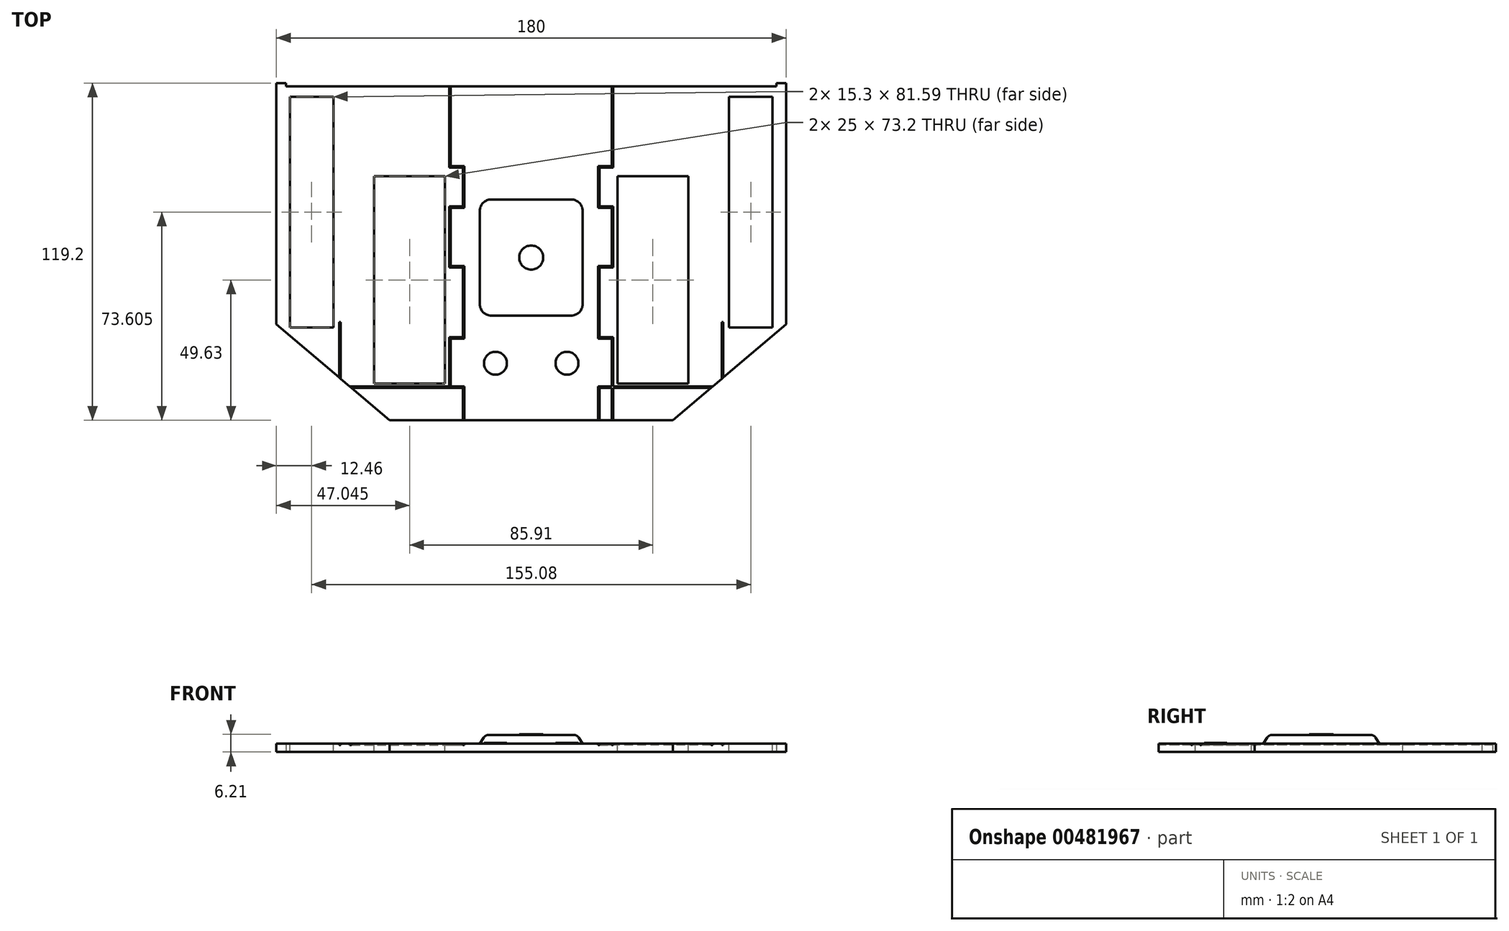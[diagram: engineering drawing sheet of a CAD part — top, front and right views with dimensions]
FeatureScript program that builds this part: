
annotation { "Feature Type Name" : "Feature", "Feature Type Description" : "" }
export const myFeature = defineFeature(function(context is Context, id is Id, definition is map)
    precondition{}
    {
        {
            var Q0;
            Q0=qCreatedBy(makeId("Top.planeOp"),FACE);
            var sketch = newSketch(context, id + "F0", { "sketchPlane" : qUnion([Q0])});
            skLineSegment(sketch, "E0", {"start": v(-90, 48.44) * mm, "end": v(-86.6, 48.44) * mm});
            skLineSegment(sketch, "E1", {"start": v(90, 48.44) * mm, "end": v(90, -36.76) * mm});
            skLineSegment(sketch, "E2", {"start": v(90, -36.76) * mm, "end": v(50, -70.76) * mm});
            skLineSegment(sketch, "E3", {"start": v(50, -70.76) * mm, "end": v(-50, -70.76) * mm});
            skLineSegment(sketch, "E4", {"start": v(-50, -70.76) * mm, "end": v(-90, -36.76) * mm});
            skLineSegment(sketch, "E5", {"start": v(-90, -36.76) * mm, "end": v(-90, 48.44) * mm});
            skLineSegment(sketch, "E6.0", {"start": v(-86.6, 47.34) * mm, "end": v(86.6, 47.34) * mm});
            skLineSegment(sketch, "E7.0", {"start": v(86.6, 48.44) * mm, "end": v(86.6, 47.34) * mm});
            skLineSegment(sketch, "E8.0", {"start": v(-86.6, 47.34) * mm, "end": v(-86.6, 48.44) * mm});
            skLineSegment(sketch, "E9.trimOffspring", {"start": v(86.6, 48.44) * mm, "end": v(90, 48.44) * mm});
            skLineSegment(sketch, "E10", {"start": v(0, 47.34) * mm, "end": v(0, -70.76) * mm, "construction": true});
            skSolve(sketch);
        }
        {
            var Q0;
            Q0 = qSketchRegion(id + "F0", true);
            extrude(context, id + "F1", {"entities" : qUnion([Q0]), "depth" : 3 * mm});
        }
        {
            var Q0;
            Q0=makeQuery(id+"F1.opExtrude","CAP_FACE",FACE,{"disambiguationData":[OSD([sQuery(id+"F0.wireOp",EDGE,"E0"),sQuery(id+"F0.wireOp",EDGE,"E1"),sQuery(id+"F0.wireOp",EDGE,"E2"),sQuery(id+"F0.wireOp",EDGE,"E3"),sQuery(id+"F0.wireOp",EDGE,"E4"),sQuery(id+"F0.wireOp",EDGE,"E5"),sQuery(id+"F0.wireOp",EDGE,"E6.0"),sQuery(id+"F0.wireOp",EDGE,"E7.0"),sQuery(id+"F0.wireOp",EDGE,"E8.0"),sQuery(id+"F0.wireOp",EDGE,"E9.trimOffspring")])],"isStart":false});
            var sketch = newSketch(context, id + "F2", { "sketchPlane" : qUnion([Q0])});
            skLineSegment(sketch, "E11", {"start": v(0, 47.34) * mm, "end": v(0, -70.76) * mm, "construction": true});
            skLineSegment(sketch, "E12", {"start": v(28.9, 47.34) * mm, "end": v(-28.9, 47.34) * mm});
            skLineSegment(sketch, "E13", {"start": v(28.9, 47.34) * mm, "end": v(28.9, 18.62) * mm});
            skLineSegment(sketch, "E14", {"start": v(28.9, 18.62) * mm, "end": v(24.1, 18.62) * mm});
            skLineSegment(sketch, "E15", {"start": v(24.1, 18.62) * mm, "end": v(24.1, 4.84) * mm});
            skLineSegment(sketch, "E16", {"start": v(24.1, 4.84) * mm, "end": v(28.9, 4.84) * mm});
            skLineSegment(sketch, "E17", {"start": v(28.9, 4.84) * mm, "end": v(28.9, -16.68) * mm});
            skLineSegment(sketch, "E18", {"start": v(28.9, -16.68) * mm, "end": v(24.1, -16.68) * mm});
            skLineSegment(sketch, "E19", {"start": v(24.1, -16.68) * mm, "end": v(24.1, -41.33) * mm});
            skLineSegment(sketch, "E20", {"start": v(24.1, -41.33) * mm, "end": v(28.9, -41.33) * mm});
            skLineSegment(sketch, "E21", {"start": v(28.9, -41.33) * mm, "end": v(28.9, -58.78) * mm});
            skLineSegment(sketch, "E22", {"start": v(67.82, -59.28) * mm, "end": v(28.9, -59.28) * mm});
            skLineSegment(sketch, "E23", {"start": v(24.1, -59.28) * mm, "end": v(24.1, -70.76) * mm});
            skLineSegment(sketch, "E24.0", {"start": v(23.6, -58.78) * mm, "end": v(23.6, -70.76) * mm});
            skLineSegment(sketch, "E24.1", {"start": v(23.6, 4.34) * mm, "end": v(28.4, 4.34) * mm});
            skLineSegment(sketch, "E24.2", {"start": v(23.6, 19.12) * mm, "end": v(23.6, 4.34) * mm});
            skLineSegment(sketch, "E24.3", {"start": v(28.4, 19.12) * mm, "end": v(23.6, 19.12) * mm});
            skLineSegment(sketch, "E24.4", {"start": v(28.4, 47.34) * mm, "end": v(28.4, 19.12) * mm});
            skLineSegment(sketch, "E24.5", {"start": v(28.4, 4.34) * mm, "end": v(28.4, -16.18) * mm});
            skLineSegment(sketch, "E24.6", {"start": v(28.4, -16.18) * mm, "end": v(23.6, -16.18) * mm});
            skLineSegment(sketch, "E24.7", {"start": v(23.6, -16.18) * mm, "end": v(23.6, -41.83) * mm});
            skLineSegment(sketch, "E24.8", {"start": v(23.6, -41.83) * mm, "end": v(28.4, -41.83) * mm});
            skLineSegment(sketch, "E24.9", {"start": v(28.4, -41.83) * mm, "end": v(28.4, -58.78) * mm});
            skLineSegment(sketch, "E24.10", {"start": v(67.32, -58.78) * mm, "end": v(28.9, -58.78) * mm});
            skLineSegment(sketch, "E25", {"start": v(23.6, -70.76) * mm, "end": v(24.1, -70.76) * mm});
            skLineSegment(sketch, "E26", {"start": v(28.4, 47.34) * mm, "end": v(28.9, 47.34) * mm});
            skLineSegment(sketch, "E27.MirrorCS", {"start": v(-28.4, 47.34) * mm, "end": v(-28.9, 47.34) * mm});
            skLineSegment(sketch, "E28.MirrorCS", {"start": v(-28.9, -16.68) * mm, "end": v(-24.1, -16.68) * mm});
            skLineSegment(sketch, "E29.MirrorCS", {"start": v(-28.4, -16.18) * mm, "end": v(-23.6, -16.18) * mm});
            skLineSegment(sketch, "E30.MirrorCS", {"start": v(-28.4, -58.78) * mm, "end": v(-23.6, -58.78) * mm});
            skLineSegment(sketch, "E31.MirrorCS", {"start": v(-23.6, -70.76) * mm, "end": v(-24.1, -70.76) * mm});
            skLineSegment(sketch, "E32.MirrorCS", {"start": v(-28.9, 18.62) * mm, "end": v(-24.1, 18.62) * mm});
            skLineSegment(sketch, "E33.MirrorCS", {"start": v(-24.1, 4.84) * mm, "end": v(-28.9, 4.84) * mm});
            skLineSegment(sketch, "E34.MirrorCS", {"start": v(-28.4, 19.12) * mm, "end": v(-23.6, 19.12) * mm});
            skLineSegment(sketch, "E35.MirrorCS", {"start": v(-24.1, -41.33) * mm, "end": v(-28.9, -41.33) * mm});
            skLineSegment(sketch, "E36.MirrorCS", {"start": v(-28.9, -59.28) * mm, "end": v(-24.1, -59.28) * mm});
            skLineSegment(sketch, "E37.MirrorCS", {"start": v(-23.6, 4.34) * mm, "end": v(-28.4, 4.34) * mm});
            skLineSegment(sketch, "E38.MirrorCS", {"start": v(-23.6, -41.83) * mm, "end": v(-28.4, -41.83) * mm});
            skLineSegment(sketch, "E39.MirrorCS", {"start": v(-28.9, 47.34) * mm, "end": v(-28.9, 18.62) * mm});
            skLineSegment(sketch, "E40.MirrorCS", {"start": v(-23.6, -58.78) * mm, "end": v(-23.6, -70.76) * mm});
            skLineSegment(sketch, "E41.MirrorCS", {"start": v(-24.1, -59.28) * mm, "end": v(-24.1, -70.76) * mm});
            skLineSegment(sketch, "E42.MirrorCS", {"start": v(-28.9, -41.33) * mm, "end": v(-28.9, -59.28) * mm});
            skLineSegment(sketch, "E43.MirrorCS", {"start": v(-28.9, 4.84) * mm, "end": v(-28.9, -16.68) * mm});
            skLineSegment(sketch, "E44.MirrorCS", {"start": v(-23.6, 19.12) * mm, "end": v(-23.6, 4.34) * mm});
            skLineSegment(sketch, "E45.MirrorCS", {"start": v(-23.6, -16.18) * mm, "end": v(-23.6, -41.83) * mm});
            skLineSegment(sketch, "E46.MirrorCS", {"start": v(-28.4, -41.83) * mm, "end": v(-28.4, -58.78) * mm});
            skLineSegment(sketch, "E47.MirrorCS", {"start": v(-28.4, 4.34) * mm, "end": v(-28.4, -16.18) * mm});
            skLineSegment(sketch, "E48.MirrorCS", {"start": v(-24.1, -16.68) * mm, "end": v(-24.1, -41.33) * mm});
            skLineSegment(sketch, "E49.MirrorCS", {"start": v(-28.4, 47.34) * mm, "end": v(-28.4, 19.12) * mm});
            skLineSegment(sketch, "E50.MirrorCS", {"start": v(-24.1, 18.62) * mm, "end": v(-24.1, 4.84) * mm});
            skPoint(sketch, "E51.orphan", {"position": v(28.9, -59.28) * mm});
            skPoint(sketch, "E52.orphan", {"position": v(28.4, -58.78) * mm});
            skLineSegment(sketch, "E53", {"start": v(67.32, -58.78) * mm, "end": v(67.32, -36) * mm});
            skLineSegment(sketch, "E54.0", {"start": v(67.82, -59.28) * mm, "end": v(67.82, -36) * mm});
            skLineSegment(sketch, "E55", {"start": v(67.32, -36) * mm, "end": v(67.82, -36) * mm});
            skLineSegment(sketch, "E56.trimOffspring", {"start": v(28.4, -58.78) * mm, "end": v(23.6, -58.78) * mm});
            skLineSegment(sketch, "E57.trimOffspring", {"start": v(28.4, -59.28) * mm, "end": v(28.4, -71.66) * mm});
            skLineSegment(sketch, "E58.trimOffspring", {"start": v(28.4, -59.28) * mm, "end": v(24.1, -59.28) * mm});
            skLineSegment(sketch, "E59.trimOffspring", {"start": v(28.9, -59.28) * mm, "end": v(28.9, -71.7) * mm});
            skLineSegment(sketch, "E60", {"start": v(28.4, -71.66) * mm, "end": v(28.9, -71.7) * mm});
            skLineSegment(sketch, "E61.MirrorCS", {"start": v(-67.32, -36) * mm, "end": v(-67.82, -36) * mm});
            skLineSegment(sketch, "E62.MirrorCS", {"start": v(-67.32, -58.78) * mm, "end": v(-67.32, -36) * mm});
            skLineSegment(sketch, "E63.MirrorCS", {"start": v(-67.82, -59.28) * mm, "end": v(-67.82, -36) * mm});
            skLineSegment(sketch, "E64.MirrorCS", {"start": v(-67.82, -59.28) * mm, "end": v(-28.9, -59.28) * mm});
            skLineSegment(sketch, "E65.MirrorCS", {"start": v(-67.32, -58.78) * mm, "end": v(-28.9, -58.78) * mm});
            skLineSegment(sketch, "E66.MirrorCS", {"start": v(-28.4, -59.28) * mm, "end": v(-28.4, -71.66) * mm});
            skLineSegment(sketch, "E67.MirrorCS", {"start": v(-28.9, -59.28) * mm, "end": v(-28.9, -71.7) * mm});
            skSolve(sketch);
        }
        {
            var Q0;
            Q0 = qSketchRegion(id + "F2", true);
            extrude(context, id + "F3", {"entities" : qUnion([Q0]), "operationType" : NewBodyOperationType.REMOVE, "oppositeDirection" : true, "depth" : .5 * mm});
        }
        {
            var Q0;
            {var subQ0=sQuery(id+"F0.wireOp",EDGE,"E6.0");var subQ1=sQuery(id+"F0.wireOp",EDGE,"E3");Q0=makeQuery(id+"F3.boolean.opBoolean","SPLIT",FACE,{"disambiguationData":[TD([makeQuery(id+"F3.opExtrude","SWEPT_FACE",FACE,{"disambiguationData":[OSD([sQuery(id+"F2.wireOp",EDGE,"E24.0")])]})])],"derivedFrom":makeQuery(id+"F1.opExtrude","CAP_FACE",FACE,{"disambiguationData":[OSD([sQuery(id+"F0.wireOp",EDGE,"E0"),sQuery(id+"F0.wireOp",EDGE,"E1"),sQuery(id+"F0.wireOp",EDGE,"E2"),subQ1,sQuery(id+"F0.wireOp",EDGE,"E4"),sQuery(id+"F0.wireOp",EDGE,"E5"),subQ0,sQuery(id+"F0.wireOp",EDGE,"E7.0"),sQuery(id+"F0.wireOp",EDGE,"E8.0"),sQuery(id+"F0.wireOp",EDGE,"E9.trimOffspring")])],"isStart":false})});}
            var sketch = newSketch(context, id + "F4", { "sketchPlane" : qUnion([Q0])});
            skLineSegment(sketch, "E68", {"start": v(0, -70.76) * mm, "end": v(0, -13.21) * mm, "construction": true});
            skPoint(sketch, "E68.endSnap0", {"position": v(0, -70.76) * mm});
            skLineSegment(sketch, "E69.bottom", {"start": v(-14.12, 7.31) * mm, "end": v(14.11, 7.31) * mm});
            skLineSegment(sketch, "E69.top", {"start": v(-14.12, -33.74) * mm, "end": v(14.11, -33.74) * mm});
            skLineSegment(sketch, "E69.left", {"start": v(-18.16, 3.27) * mm, "end": v(-18.16, -29.7) * mm});
            skLineSegment(sketch, "E69.right", {"start": v(18.16, 3.27) * mm, "end": v(18.15, -29.7) * mm});
            skPoint(sketch, "E69.middle", {"position": v(0, -13.21) * mm});
            skPoint(sketch, "E70.visualSharp", {"position": v(-18.16, 7.31) * mm});
            skArc(sketch, "E70.filletArc", {"start": v(-14.12, 7.31) * mm, "mid": v(-16.97, 6.13) * mm, "end": v(-18.16, 3.27) * mm});
            skPoint(sketch, "E71.visualSharp", {"position": v(18.16, 7.31) * mm});
            skArc(sketch, "E71.filletArc", {"start": v(18.15, 3.27) * mm, "mid": v(16.97, 6.13) * mm, "end": v(14.11, 7.31) * mm});
            skPoint(sketch, "E72.visualSharp", {"position": v(18.15, -33.74) * mm});
            skArc(sketch, "E72.filletArc", {"start": v(14.11, -33.74) * mm, "mid": v(16.97, -32.55) * mm, "end": v(18.16, -29.7) * mm});
            skPoint(sketch, "E73.visualSharp", {"position": v(-18.16, -33.74) * mm});
            skArc(sketch, "E73.filletArc", {"start": v(-18.16, -29.7) * mm, "mid": v(-16.97, -32.55) * mm, "end": v(-14.12, -33.74) * mm});
            skSolve(sketch);
        }
        {
            var Q0;
            Q0 = qSketchRegion(id + "F4", true);
            extrude(context, id + "F5", {"entities" : qUnion([Q0]), "operationType" : NewBodyOperationType.ADD, "depth" : 3 * mm});
        }
        {
            var Q0;
            Q0=makeQuery(id+"F5.opExtrude","CAP_EDGE",EDGE,{"disambiguationData":[OSD([sQuery(id+"F4.wireOp",EDGE,"E69.left")])],"isStart":false});
            chamfer(context, id + "F6", {"entities" : qUnion([Q0]), "chamferType" : ChamferType.TWO_OFFSETS, "width1" : 2 * mm, "oppositeDirection" : false, "width2" : 3 * mm, "tangentPropagation" : true});
        }
        {
            var Q0;
            {var subQ0=sQuery(id+"F4.wireOp",EDGE,"E71.filletArc");Q0=makeQuery(id+"F6.opChamfer","BLEND_EDGE",EDGE,{"blendedFrom":[makeQuery(id+"F5.opExtrude","CAP_EDGE",EDGE,{"disambiguationData":[OSD([subQ0])],"isStart":false}),makeQuery(id+"F5.opExtrude","CAP_FACE",FACE,{"disambiguationData":[OSD([sQuery(id+"F4.wireOp",EDGE,"E69.bottom"),sQuery(id+"F4.wireOp",EDGE,"E69.top"),sQuery(id+"F4.wireOp",EDGE,"E69.left"),sQuery(id+"F4.wireOp",EDGE,"E69.right"),sQuery(id+"F4.wireOp",EDGE,"E70.filletArc"),subQ0,sQuery(id+"F4.wireOp",EDGE,"E72.filletArc"),sQuery(id+"F4.wireOp",EDGE,"E73.filletArc")])],"isStart":false})],"blendedInto":[makeQuery(id+"F5.opExtrude","CAP_FACE",FACE,{"disambiguationData":[OSD([sQuery(id+"F4.wireOp",EDGE,"E69.bottom"),sQuery(id+"F4.wireOp",EDGE,"E69.top"),sQuery(id+"F4.wireOp",EDGE,"E69.left"),sQuery(id+"F4.wireOp",EDGE,"E69.right"),sQuery(id+"F4.wireOp",EDGE,"E70.filletArc"),subQ0,sQuery(id+"F4.wireOp",EDGE,"E72.filletArc"),sQuery(id+"F4.wireOp",EDGE,"E73.filletArc")])],"isStart":false})]});}
            fillet(context, id + "F7", {"entities" : qUnion([Q0]), "radius" : 2 * mm, "tangentPropagation" : true, "allowEdgeOverflow" : false});
        }
        {
            var Q0;
            Q0=makeQuery(id+"F5.opExtrude","CAP_FACE",FACE,{"disambiguationData":[OSD([sQuery(id+"F4.wireOp",EDGE,"E69.bottom"),sQuery(id+"F4.wireOp",EDGE,"E69.top"),sQuery(id+"F4.wireOp",EDGE,"E69.left"),sQuery(id+"F4.wireOp",EDGE,"E69.right"),sQuery(id+"F4.wireOp",EDGE,"E70.filletArc"),sQuery(id+"F4.wireOp",EDGE,"E71.filletArc"),sQuery(id+"F4.wireOp",EDGE,"E72.filletArc"),sQuery(id+"F4.wireOp",EDGE,"E73.filletArc")])],"isStart":false});
            var sketch = newSketch(context, id + "F8", { "sketchPlane" : qUnion([Q0])});
            skLineSegment(sketch, "E74", {"start": v(0, -30.66) * mm, "end": v(0, 4.24) * mm, "construction": true});
            skCircle(sketch, "E75", {"center": v(0, -13.21) * mm, "radius": 4.25 * mm});
            skSolve(sketch);
        }
        {
            var Q0;
            Q0 = qSketchRegion(id + "F8", true);
            extrude(context, id + "F9", {"entities" : qUnion([Q0]), "operationType" : NewBodyOperationType.ADD, "depth" : .2 * mm});
        }
        {
            var Q0;
            {var subQ0=sQuery(id+"F0.wireOp",EDGE,"E6.0");var subQ1=sQuery(id+"F0.wireOp",EDGE,"E3");Q0=makeQuery(id+"F3.boolean.opBoolean","SPLIT",FACE,{"disambiguationData":[TD([makeQuery(id+"F3.opExtrude","SWEPT_FACE",FACE,{"disambiguationData":[OSD([sQuery(id+"F2.wireOp",EDGE,"E24.0")])]})])],"derivedFrom":makeQuery(id+"F1.opExtrude","CAP_FACE",FACE,{"disambiguationData":[OSD([sQuery(id+"F0.wireOp",EDGE,"E0"),sQuery(id+"F0.wireOp",EDGE,"E1"),sQuery(id+"F0.wireOp",EDGE,"E2"),subQ1,sQuery(id+"F0.wireOp",EDGE,"E4"),sQuery(id+"F0.wireOp",EDGE,"E5"),subQ0,sQuery(id+"F0.wireOp",EDGE,"E7.0"),sQuery(id+"F0.wireOp",EDGE,"E8.0"),sQuery(id+"F0.wireOp",EDGE,"E9.trimOffspring")])],"isStart":false})});}
            var sketch = newSketch(context, id + "F10", { "sketchPlane" : qUnion([Q0])});
            skLineSegment(sketch, "E76", {"start": v(0, -70.76) * mm, "end": v(0, -50.57) * mm, "construction": true});
            skLineSegment(sketch, "E77", {"start": v(-12.63, -50.57) * mm, "end": v(12.63, -50.57) * mm, "construction": true});
            skCircle(sketch, "E78", {"center": v(-12.63, -50.57) * mm, "radius": 4.04 * mm});
            skCircle(sketch, "E79", {"center": v(12.63, -50.57) * mm, "radius": 4.04 * mm});
            skSolve(sketch);
        }
        {
            var Q0;
            Q0 = qSketchRegion(id + "F10", true);
            extrude(context, id + "F11", {"entities" : qUnion([Q0]), "operationType" : NewBodyOperationType.ADD, "depth" : .2 * mm});
        }
        {
            var Q0;
            {var subQ0=sQuery(id+"F0.wireOp",EDGE,"E8.0");var subQ1=sQuery(id+"F0.wireOp",EDGE,"E6.0");var subQ2=sQuery(id+"F0.wireOp",EDGE,"E0");var subQ3=sQuery(id+"F0.wireOp",EDGE,"E3");var subQ4=sQuery(id+"F0.wireOp",EDGE,"E4");var subQ5=sQuery(id+"F0.wireOp",EDGE,"E5");Q0=makeQuery(id+"F3.boolean.opBoolean","SPLIT",FACE,{"disambiguationData":[TD([makeQuery(id+"F1.opExtrude","SWEPT_FACE",FACE,{"disambiguationData":[OSD([subQ2])]})])],"derivedFrom":makeQuery(id+"F1.opExtrude","CAP_FACE",FACE,{"disambiguationData":[OSD([subQ2,sQuery(id+"F0.wireOp",EDGE,"E1"),sQuery(id+"F0.wireOp",EDGE,"E2"),subQ3,subQ4,subQ5,subQ1,sQuery(id+"F0.wireOp",EDGE,"E7.0"),subQ0,sQuery(id+"F0.wireOp",EDGE,"E9.trimOffspring")])],"isStart":false})});}
            var sketch = newSketch(context, id + "F12", { "sketchPlane" : qUnion([Q0])});
            skLineSegment(sketch, "E80", {"start": v(0, 0) * mm, "end": v(0, -56.54) * mm, "construction": true});
            skLineSegment(sketch, "E81.bottom", {"start": v(-85.19, 43.64) * mm, "end": v(-69.9, 43.64) * mm});
            skLineSegment(sketch, "E81.top", {"start": v(-85.19, -37.95) * mm, "end": v(-69.9, -37.95) * mm});
            skLineSegment(sketch, "E81.left", {"start": v(-85.2, 43.64) * mm, "end": v(-85.19, -37.95) * mm});
            skLineSegment(sketch, "E81.right", {"start": v(-69.89, 43.64) * mm, "end": v(-69.89, -37.95) * mm});
            skLineSegment(sketch, "E82.MirrorCS", {"start": v(69.89, 43.64) * mm, "end": v(69.89, -37.95) * mm});
            skLineSegment(sketch, "E83.MirrorCS", {"start": v(85.19, 43.64) * mm, "end": v(69.89, 43.64) * mm});
            skLineSegment(sketch, "E84.MirrorCS", {"start": v(85.19, 43.64) * mm, "end": v(85.19, -37.95) * mm});
            skLineSegment(sketch, "E85.MirrorCS", {"start": v(85.19, -37.95) * mm, "end": v(69.9, -37.95) * mm});
            skLineSegment(sketch, "E86.0", {"start": v(-55.45, -57.73) * mm, "end": v(-55.46, 15.47) * mm});
            skLineSegment(sketch, "E86.1", {"start": v(-30.45, -57.73) * mm, "end": v(-55.45, -57.73) * mm});
            skLineSegment(sketch, "E86.2", {"start": v(-30.45, -57.73) * mm, "end": v(-30.46, 15.47) * mm});
            skLineSegment(sketch, "E86.3", {"start": v(-30.46, 15.47) * mm, "end": v(-55.46, 15.47) * mm});
            skLineSegment(sketch, "E87.MirrorCS", {"start": v(30.45, -57.73) * mm, "end": v(30.46, 15.47) * mm});
            skLineSegment(sketch, "E88.MirrorCS", {"start": v(30.46, 15.47) * mm, "end": v(55.46, 15.47) * mm});
            skLineSegment(sketch, "E89.MirrorCS", {"start": v(55.45, -57.73) * mm, "end": v(55.46, 15.47) * mm});
            skLineSegment(sketch, "E90.MirrorCS", {"start": v(30.45, -57.73) * mm, "end": v(55.45, -57.73) * mm});
            skSolve(sketch);
        }
        {
            var Q0;
            Q0 = qSketchRegion(id + "F12", true);
            extrude(context, id + "F13", {"entities" : qUnion([Q0]), "operationType" : NewBodyOperationType.REMOVE, "oppositeDirection" : true, "depth" : 25 * mm});
        }
    });
